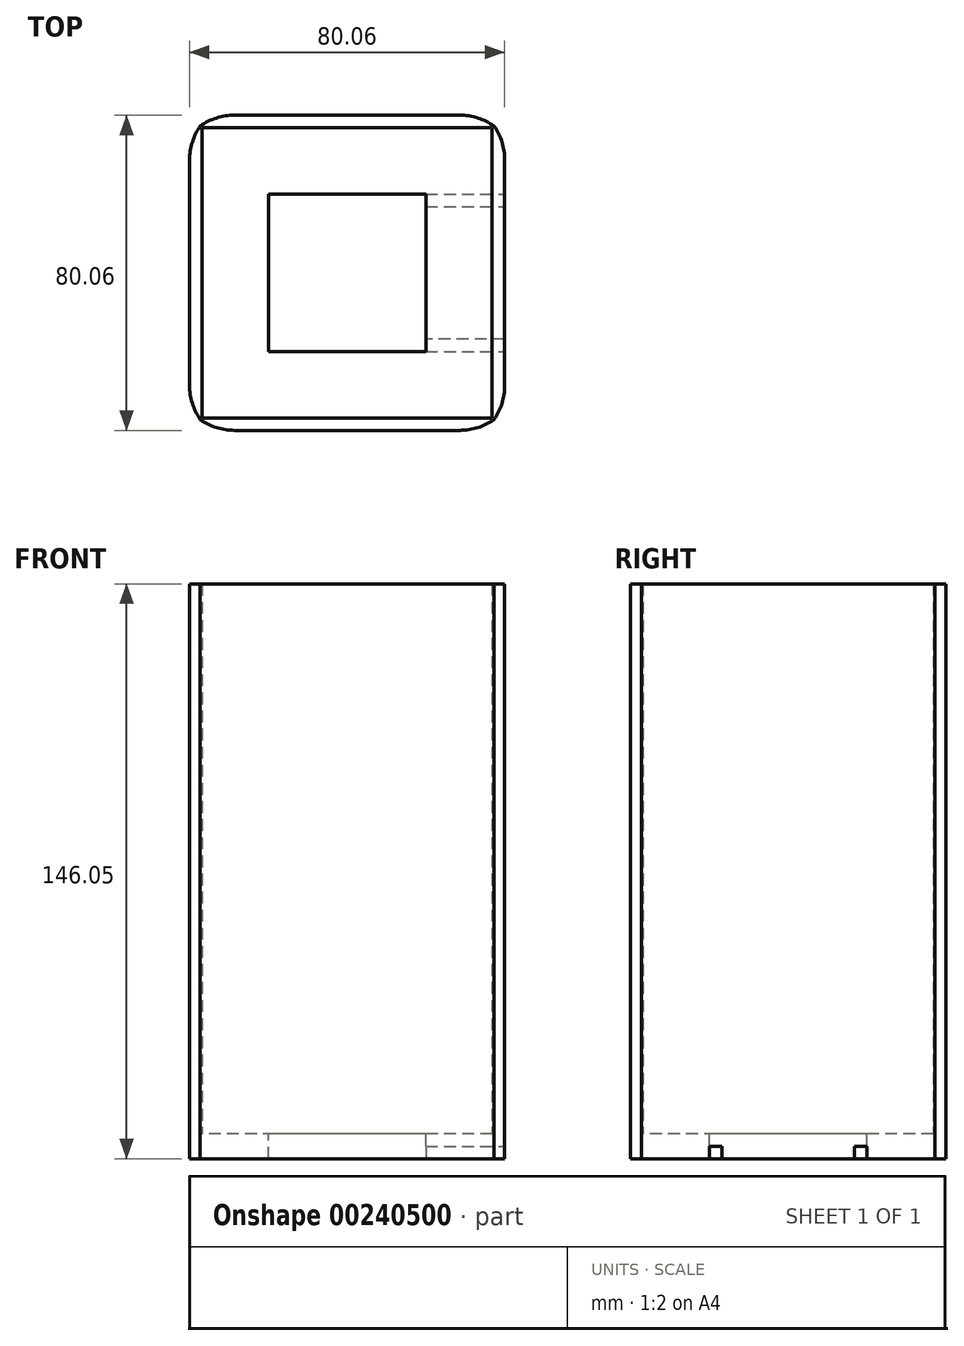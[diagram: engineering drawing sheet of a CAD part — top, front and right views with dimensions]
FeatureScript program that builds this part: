
annotation { "Feature Type Name" : "Feature", "Feature Type Description" : "" }
export const myFeature = defineFeature(function(context is Context, id is Id, definition is map)
    precondition{}
    {
        {
            var Q0;
            Q0=qCreatedBy(makeId("Top.planeOp"),FACE);
            var sketch = newSketch(context, id + "F0", { "sketchPlane" : qUnion([Q0])});
            skLineSegment(sketch, "E0.bottom", {"start": v(20, 20) * mm, "end": v(-20, 20) * mm});
            skLineSegment(sketch, "E0.top", {"start": v(20, -20) * mm, "end": v(-20, -20) * mm});
            skLineSegment(sketch, "E0.left", {"start": v(20, 20) * mm, "end": v(20, -20) * mm});
            skLineSegment(sketch, "E0.right", {"start": v(-20, 20) * mm, "end": v(-20, -20) * mm});
            skPoint(sketch, "E0.middle", {"position": v(0, 0) * mm});
            skLineSegment(sketch, "E1.bottom", {"start": v(36.85, 36.85) * mm, "end": v(-36.85, 36.85) * mm});
            skLineSegment(sketch, "E1.top", {"start": v(36.85, -36.85) * mm, "end": v(-36.85, -36.85) * mm});
            skLineSegment(sketch, "E1.left", {"start": v(36.85, 36.85) * mm, "end": v(36.85, -36.85) * mm});
            skLineSegment(sketch, "E1.right", {"start": v(-36.85, 36.85) * mm, "end": v(-36.85, -36.85) * mm});
            skLineSegment(sketch, "E2.bottom", {"start": v(-40.03, 40.03) * mm, "end": v(40.03, 40.03) * mm});
            skLineSegment(sketch, "E2.top", {"start": v(-40.03, -40.03) * mm, "end": v(40.03, -40.03) * mm});
            skLineSegment(sketch, "E2.left", {"start": v(-40.03, 40.03) * mm, "end": v(-40.03, -40.03) * mm});
            skLineSegment(sketch, "E2.right", {"start": v(40.03, 40.03) * mm, "end": v(40.03, -40.03) * mm});
            skSolve(sketch);
        }
        {
            var Q0;
            Q0=makeQuery(id+"F0.imprint","IMPRINT",FACE,{"disambiguationData":[TD([[makeQuery(id+"F0.imprint","IMPRINT",EDGE,{"derivedFrom":sQuery(id+"F0.wireOp",EDGE,"E0.bottom")}),-1.0]])]});
            var Q1;
            Q1=makeQuery(id+"F0.imprint","IMPRINT",FACE,{"disambiguationData":[TD([[makeQuery(id+"F0.imprint","IMPRINT",EDGE,{"derivedFrom":sQuery(id+"F0.wireOp",EDGE,"E0.bottom")}),1.0]])]});
            var Q2;
            Q2=makeQuery(id+"F0.imprint","IMPRINT",FACE,{"disambiguationData":[TD([[makeQuery(id+"F0.imprint","IMPRINT",EDGE,{"derivedFrom":sQuery(id+"F0.wireOp",EDGE,"E1.bottom")}),-1.0]])]});
            extrude(context, id + "F1", {"entities" : qUnion([Q0, Q1, Q2]), "oppositeDirection" : true, "depth" : 6.35 * mm});
        }
        {
            var Q0;
            Q0=makeQuery(id+"F0.imprint","IMPRINT",FACE,{"disambiguationData":[TD([[makeQuery(id+"F0.imprint","IMPRINT",EDGE,{"derivedFrom":sQuery(id+"F0.wireOp",EDGE,"E0.bottom")}),1.0]])]});
            extrude(context, id + "F2", {"entities" : qUnion([Q0]), "operationType" : NewBodyOperationType.REMOVE, "oppositeDirection" : true, "depth" : 9.14 * mm});
        }
        {
            var Q0;
            Q0=makeQuery(id+"F0.imprint","IMPRINT",FACE,{"disambiguationData":[TD([[makeQuery(id+"F0.imprint","IMPRINT",EDGE,{"derivedFrom":sQuery(id+"F0.wireOp",EDGE,"E1.bottom")}),-1.0]])]});
            extrude(context, id + "F3", {"entities" : qUnion([Q0]), "operationType" : NewBodyOperationType.ADD, "depth" : 139.7 * mm});
        }
        {
            var Q0;
            Q0=makeQuery(id+"F1.opExtrude","CAP_FACE",FACE,{"disambiguationData":[OSD([sQuery(id+"F0.wireOp",EDGE,"E2.bottom"),sQuery(id+"F0.wireOp",EDGE,"E2.top"),sQuery(id+"F0.wireOp",EDGE,"E2.left"),sQuery(id+"F0.wireOp",EDGE,"E2.right")])],"isStart":false});
            var sketch = newSketch(context, id + "F4", { "sketchPlane" : qUnion([Q0])});
            skLineSegment(sketch, "E3", {"start": v(20, 20) * mm, "end": v(40.03, 20) * mm});
            skLineSegment(sketch, "E4", {"start": v(40.03, 16.82) * mm, "end": v(20, 16.82) * mm});
            skLineSegment(sketch, "E5", {"start": v(20, -20) * mm, "end": v(40.03, -20) * mm});
            skLineSegment(sketch, "E6", {"start": v(20, -16.82) * mm, "end": v(40.03, -16.82) * mm});
            skSolve(sketch);
        }
        {
            var Q0;
            {var subQ0=sQuery(id+"F4.wireOp",EDGE,"E3");Q0=makeQuery(id+"F4.imprint","IMPRINT",FACE,{"disambiguationData":[TD([[makeQuery(id+"F4.imprint","IMPRINT",EDGE,{"derivedFrom":subQ0}),-1.0]])]});}
            var Q1;
            {var subQ0=sQuery(id+"F4.wireOp",EDGE,"E5");Q1=makeQuery(id+"F4.imprint","IMPRINT",FACE,{"disambiguationData":[TD([[makeQuery(id+"F4.imprint","IMPRINT",EDGE,{"derivedFrom":subQ0}),1.0]])]});}
            extrude(context, id + "F5", {"entities" : qUnion([Q0, Q1]), "operationType" : NewBodyOperationType.REMOVE, "oppositeDirection" : true, "depth" : 3.17 * mm});
        }
        {
            var Q0;
            {var subQ0=sQuery(id+"F0.wireOp",EDGE,"E2.right");var subQ1=sQuery(id+"F0.wireOp",EDGE,"E2.top");Q0=makeQuery(id+"F3.boolean.opBoolean","MERGE",EDGE,{"derivedFrom":[makeQuery(id+"F1.opExtrude","SWEPT_EDGE",EDGE,{"disambiguationData":[OSD([subQ1,subQ0])]}),makeQuery(id+"F3.opExtrude","SWEPT_EDGE",EDGE,{"disambiguationData":[OSD([subQ1,subQ0])]})]});}
            var Q1;
            {var subQ0=sQuery(id+"F0.wireOp",EDGE,"E2.left");var subQ1=sQuery(id+"F0.wireOp",EDGE,"E2.top");Q1=makeQuery(id+"F3.boolean.opBoolean","MERGE",EDGE,{"derivedFrom":[makeQuery(id+"F1.opExtrude","SWEPT_EDGE",EDGE,{"disambiguationData":[OSD([subQ1,subQ0])]}),makeQuery(id+"F3.opExtrude","SWEPT_EDGE",EDGE,{"disambiguationData":[OSD([subQ1,subQ0])]})]});}
            var Q2;
            {var subQ0=sQuery(id+"F0.wireOp",EDGE,"E2.left");var subQ1=sQuery(id+"F0.wireOp",EDGE,"E2.bottom");Q2=makeQuery(id+"F3.boolean.opBoolean","MERGE",EDGE,{"derivedFrom":[makeQuery(id+"F1.opExtrude","SWEPT_EDGE",EDGE,{"disambiguationData":[OSD([subQ1,subQ0])]}),makeQuery(id+"F3.opExtrude","SWEPT_EDGE",EDGE,{"disambiguationData":[OSD([subQ1,subQ0])]})]});}
            var Q3;
            {var subQ0=sQuery(id+"F0.wireOp",EDGE,"E2.right");var subQ1=sQuery(id+"F0.wireOp",EDGE,"E2.bottom");Q3=makeQuery(id+"F3.boolean.opBoolean","MERGE",EDGE,{"derivedFrom":[makeQuery(id+"F1.opExtrude","SWEPT_EDGE",EDGE,{"disambiguationData":[OSD([subQ1,subQ0])]}),makeQuery(id+"F3.opExtrude","SWEPT_EDGE",EDGE,{"disambiguationData":[OSD([subQ1,subQ0])]})]});}
            chamfer(context, id + "F7", {"entities" : qUnion([Q0, Q1, Q2, Q3]), "width" : 5.08 * mm, "tangentPropagation" : true});
        }
        {
            var Q0;
            {var subQ0=sQuery(id+"F0.wireOp",EDGE,"E2.top");var subQ1=sQuery(id+"F0.wireOp",EDGE,"E2.left");Q0=makeQuery(id+"F7.opChamfer","BLEND_EDGE",EDGE,{"blendedFrom":[makeQuery(id+"F3.boolean.opBoolean","MERGE",EDGE,{"derivedFrom":[makeQuery(id+"F1.opExtrude","SWEPT_EDGE",EDGE,{"disambiguationData":[OSD([subQ0,subQ1])]}),makeQuery(id+"F3.opExtrude","SWEPT_EDGE",EDGE,{"disambiguationData":[OSD([subQ0,subQ1])]})]}),makeQuery(id+"F3.boolean.opBoolean","MERGE",FACE,{"derivedFrom":[makeQuery(id+"F1.opExtrude","SWEPT_FACE",FACE,{"disambiguationData":[OSD([subQ0])]}),makeQuery(id+"F3.opExtrude","SWEPT_FACE",FACE,{"disambiguationData":[OSD([subQ0])]})]})],"blendedInto":[makeQuery(id+"F3.boolean.opBoolean","MERGE",FACE,{"derivedFrom":[makeQuery(id+"F1.opExtrude","SWEPT_FACE",FACE,{"disambiguationData":[OSD([subQ0])]}),makeQuery(id+"F3.opExtrude","SWEPT_FACE",FACE,{"disambiguationData":[OSD([subQ0])]})]})]});}
            var Q1;
            {var subQ0=sQuery(id+"F0.wireOp",EDGE,"E2.left");var subQ1=sQuery(id+"F0.wireOp",EDGE,"E2.top");Q1=makeQuery(id+"F7.opChamfer","BLEND_EDGE",EDGE,{"blendedFrom":[makeQuery(id+"F3.boolean.opBoolean","MERGE",EDGE,{"derivedFrom":[makeQuery(id+"F1.opExtrude","SWEPT_EDGE",EDGE,{"disambiguationData":[OSD([subQ1,subQ0])]}),makeQuery(id+"F3.opExtrude","SWEPT_EDGE",EDGE,{"disambiguationData":[OSD([subQ1,subQ0])]})]}),makeQuery(id+"F3.boolean.opBoolean","MERGE",FACE,{"derivedFrom":[makeQuery(id+"F1.opExtrude","SWEPT_FACE",FACE,{"disambiguationData":[OSD([subQ0])]}),makeQuery(id+"F3.opExtrude","SWEPT_FACE",FACE,{"disambiguationData":[OSD([subQ0])]})]})],"blendedInto":[makeQuery(id+"F3.boolean.opBoolean","MERGE",FACE,{"derivedFrom":[makeQuery(id+"F1.opExtrude","SWEPT_FACE",FACE,{"disambiguationData":[OSD([subQ0])]}),makeQuery(id+"F3.opExtrude","SWEPT_FACE",FACE,{"disambiguationData":[OSD([subQ0])]})]})]});}
            var Q2;
            {var subQ0=sQuery(id+"F0.wireOp",EDGE,"E2.left");var subQ1=sQuery(id+"F0.wireOp",EDGE,"E2.bottom");Q2=makeQuery(id+"F7.opChamfer","BLEND_EDGE",EDGE,{"blendedFrom":[makeQuery(id+"F3.boolean.opBoolean","MERGE",EDGE,{"derivedFrom":[makeQuery(id+"F1.opExtrude","SWEPT_EDGE",EDGE,{"disambiguationData":[OSD([subQ1,subQ0])]}),makeQuery(id+"F3.opExtrude","SWEPT_EDGE",EDGE,{"disambiguationData":[OSD([subQ1,subQ0])]})]}),makeQuery(id+"F3.boolean.opBoolean","MERGE",FACE,{"derivedFrom":[makeQuery(id+"F1.opExtrude","SWEPT_FACE",FACE,{"disambiguationData":[OSD([subQ0])]}),makeQuery(id+"F3.opExtrude","SWEPT_FACE",FACE,{"disambiguationData":[OSD([subQ0])]})]})],"blendedInto":[makeQuery(id+"F3.boolean.opBoolean","MERGE",FACE,{"derivedFrom":[makeQuery(id+"F1.opExtrude","SWEPT_FACE",FACE,{"disambiguationData":[OSD([subQ0])]}),makeQuery(id+"F3.opExtrude","SWEPT_FACE",FACE,{"disambiguationData":[OSD([subQ0])]})]})]});}
            var Q3;
            {var subQ0=sQuery(id+"F0.wireOp",EDGE,"E2.bottom");var subQ1=sQuery(id+"F0.wireOp",EDGE,"E2.left");Q3=makeQuery(id+"F7.opChamfer","BLEND_EDGE",EDGE,{"blendedFrom":[makeQuery(id+"F3.boolean.opBoolean","MERGE",EDGE,{"derivedFrom":[makeQuery(id+"F1.opExtrude","SWEPT_EDGE",EDGE,{"disambiguationData":[OSD([subQ0,subQ1])]}),makeQuery(id+"F3.opExtrude","SWEPT_EDGE",EDGE,{"disambiguationData":[OSD([subQ0,subQ1])]})]}),makeQuery(id+"F3.boolean.opBoolean","MERGE",FACE,{"derivedFrom":[makeQuery(id+"F1.opExtrude","SWEPT_FACE",FACE,{"disambiguationData":[OSD([subQ0])]}),makeQuery(id+"F3.opExtrude","SWEPT_FACE",FACE,{"disambiguationData":[OSD([subQ0])]})]})],"blendedInto":[makeQuery(id+"F3.boolean.opBoolean","MERGE",FACE,{"derivedFrom":[makeQuery(id+"F1.opExtrude","SWEPT_FACE",FACE,{"disambiguationData":[OSD([subQ0])]}),makeQuery(id+"F3.opExtrude","SWEPT_FACE",FACE,{"disambiguationData":[OSD([subQ0])]})]})]});}
            var Q4;
            {var subQ0=sQuery(id+"F0.wireOp",EDGE,"E2.right");var subQ1=sQuery(id+"F0.wireOp",EDGE,"E2.top");Q4=makeQuery(id+"F7.opChamfer","BLEND_EDGE",EDGE,{"blendedFrom":[makeQuery(id+"F3.boolean.opBoolean","MERGE",EDGE,{"derivedFrom":[makeQuery(id+"F1.opExtrude","SWEPT_EDGE",EDGE,{"disambiguationData":[OSD([subQ1,subQ0])]}),makeQuery(id+"F3.opExtrude","SWEPT_EDGE",EDGE,{"disambiguationData":[OSD([subQ1,subQ0])]})]}),makeQuery(id+"F3.boolean.opBoolean","MERGE",FACE,{"derivedFrom":[makeQuery(id+"F1.opExtrude","SWEPT_FACE",FACE,{"disambiguationData":[OSD([subQ0])]}),makeQuery(id+"F3.opExtrude","SWEPT_FACE",FACE,{"disambiguationData":[OSD([subQ0])]})]})],"blendedInto":[makeQuery(id+"F3.boolean.opBoolean","MERGE",FACE,{"derivedFrom":[makeQuery(id+"F1.opExtrude","SWEPT_FACE",FACE,{"disambiguationData":[OSD([subQ0])]}),makeQuery(id+"F3.opExtrude","SWEPT_FACE",FACE,{"disambiguationData":[OSD([subQ0])]})]})]});}
            var Q5;
            {var subQ0=sQuery(id+"F0.wireOp",EDGE,"E2.top");var subQ1=sQuery(id+"F0.wireOp",EDGE,"E2.right");Q5=makeQuery(id+"F7.opChamfer","BLEND_EDGE",EDGE,{"blendedFrom":[makeQuery(id+"F3.boolean.opBoolean","MERGE",EDGE,{"derivedFrom":[makeQuery(id+"F1.opExtrude","SWEPT_EDGE",EDGE,{"disambiguationData":[OSD([subQ0,subQ1])]}),makeQuery(id+"F3.opExtrude","SWEPT_EDGE",EDGE,{"disambiguationData":[OSD([subQ0,subQ1])]})]}),makeQuery(id+"F3.boolean.opBoolean","MERGE",FACE,{"derivedFrom":[makeQuery(id+"F1.opExtrude","SWEPT_FACE",FACE,{"disambiguationData":[OSD([subQ0])]}),makeQuery(id+"F3.opExtrude","SWEPT_FACE",FACE,{"disambiguationData":[OSD([subQ0])]})]})],"blendedInto":[makeQuery(id+"F3.boolean.opBoolean","MERGE",FACE,{"derivedFrom":[makeQuery(id+"F1.opExtrude","SWEPT_FACE",FACE,{"disambiguationData":[OSD([subQ0])]}),makeQuery(id+"F3.opExtrude","SWEPT_FACE",FACE,{"disambiguationData":[OSD([subQ0])]})]})]});}
            var Q6;
            {var subQ0=sQuery(id+"F0.wireOp",EDGE,"E2.right");var subQ1=sQuery(id+"F0.wireOp",EDGE,"E2.bottom");Q6=makeQuery(id+"F7.opChamfer","BLEND_EDGE",EDGE,{"blendedFrom":[makeQuery(id+"F3.boolean.opBoolean","MERGE",EDGE,{"derivedFrom":[makeQuery(id+"F1.opExtrude","SWEPT_EDGE",EDGE,{"disambiguationData":[OSD([subQ1,subQ0])]}),makeQuery(id+"F3.opExtrude","SWEPT_EDGE",EDGE,{"disambiguationData":[OSD([subQ1,subQ0])]})]}),makeQuery(id+"F3.boolean.opBoolean","MERGE",FACE,{"derivedFrom":[makeQuery(id+"F1.opExtrude","SWEPT_FACE",FACE,{"disambiguationData":[OSD([subQ0])]}),makeQuery(id+"F3.opExtrude","SWEPT_FACE",FACE,{"disambiguationData":[OSD([subQ0])]})]})],"blendedInto":[makeQuery(id+"F3.boolean.opBoolean","MERGE",FACE,{"derivedFrom":[makeQuery(id+"F1.opExtrude","SWEPT_FACE",FACE,{"disambiguationData":[OSD([subQ0])]}),makeQuery(id+"F3.opExtrude","SWEPT_FACE",FACE,{"disambiguationData":[OSD([subQ0])]})]})]});}
            var Q7;
            {var subQ0=sQuery(id+"F0.wireOp",EDGE,"E2.bottom");var subQ1=sQuery(id+"F0.wireOp",EDGE,"E2.right");Q7=makeQuery(id+"F7.opChamfer","BLEND_EDGE",EDGE,{"blendedFrom":[makeQuery(id+"F3.boolean.opBoolean","MERGE",EDGE,{"derivedFrom":[makeQuery(id+"F1.opExtrude","SWEPT_EDGE",EDGE,{"disambiguationData":[OSD([subQ0,subQ1])]}),makeQuery(id+"F3.opExtrude","SWEPT_EDGE",EDGE,{"disambiguationData":[OSD([subQ0,subQ1])]})]}),makeQuery(id+"F3.boolean.opBoolean","MERGE",FACE,{"derivedFrom":[makeQuery(id+"F1.opExtrude","SWEPT_FACE",FACE,{"disambiguationData":[OSD([subQ0])]}),makeQuery(id+"F3.opExtrude","SWEPT_FACE",FACE,{"disambiguationData":[OSD([subQ0])]})]})],"blendedInto":[makeQuery(id+"F3.boolean.opBoolean","MERGE",FACE,{"derivedFrom":[makeQuery(id+"F1.opExtrude","SWEPT_FACE",FACE,{"disambiguationData":[OSD([subQ0])]}),makeQuery(id+"F3.opExtrude","SWEPT_FACE",FACE,{"disambiguationData":[OSD([subQ0])]})]})]});}
            fillet(context, id + "F6", {"entities" : qUnion([Q0, Q1, Q2, Q3, Q4, Q5, Q6, Q7]), "radius" : 15.24 * mm, "tangentPropagation" : true, "allowEdgeOverflow" : false});
        }
    });
